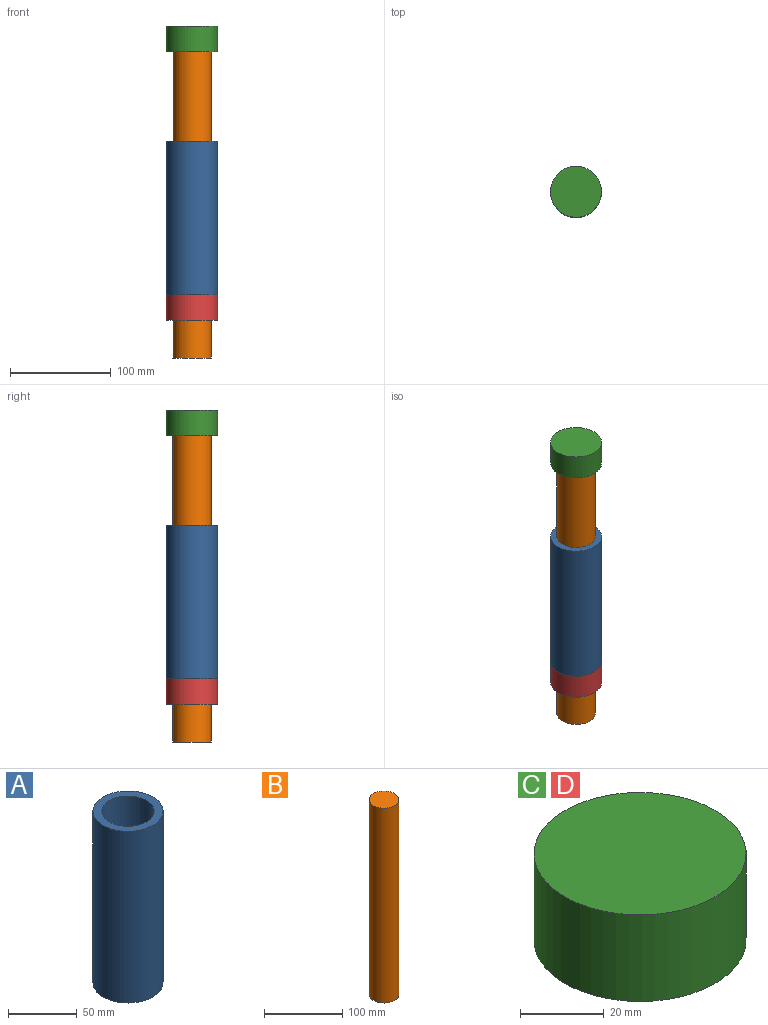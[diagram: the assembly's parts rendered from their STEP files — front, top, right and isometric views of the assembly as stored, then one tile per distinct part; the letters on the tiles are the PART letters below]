
ASSEMBLY  parts=4 mates=3
PART A: 4 faces, bbox 50.8x50.8x152.4 mm
  f0: cylinder r=25.4mm len=152.4mm, axis (0,0,-1), area 24322mm2, adj f2,f3
  f1: cylinder r=19.05mm len=152.4mm, axis (0,0,-1), area 18241.5mm2, adj f2,f3
  f2: plane 50.8x50.8mm, normal (0,0,1), area 886.7mm2, adj f0,f1
  f3: plane 50.8x50.8mm, normal (0,0,-1), area 886.7mm2, adj f0,f1
PART B: 3 faces, bbox 38.1x38.1x304.8 mm
  f0: cylinder r=19.05mm len=304.8mm, axis (0,0,-1), area 36482.9mm2, adj f1,f2
  f1: plane 38.1x38.1mm, normal (0,0,1), area 1140.1mm2, adj f0
  f2: plane 38.1x38.1mm, normal (0,0,-1), area 1140.1mm2, adj f0
PART C: 3 faces, bbox 50.8x50.8x25.4 mm
  f0: cylinder r=25.4mm len=50.8mm, axis (0,0,-1), area 4053.7mm2, adj f1,f2
  f1: plane 50.8x50.8mm, normal (0,0,1), area 2026.8mm2, adj f0
  f2: plane 50.8x50.8mm, normal (0,0,-1), area 2026.8mm2, adj f0
PART D: same geometry as C
PLACE A t=(-402.6,316.4,79.28)mm
PLACE B t=(-402.6,316.4,16.17)mm
PLACE C t=(-402.6,316.4,320.97)mm
PLACE D t=(-402.6,316.4,53.88)mm
MATE fastened C.f0 <-> B.f0  axis (0,0,-1) through (-402.6,316.4,320.97)mm
MATE fastened D.f0 <-> A.f0  axis (0,0,1) through (-402.6,316.4,79.28)mm
MATE slider B.f0 <-> D.f0  axis (0,0,-1) through (-402.6,316.4,16.17)mm
